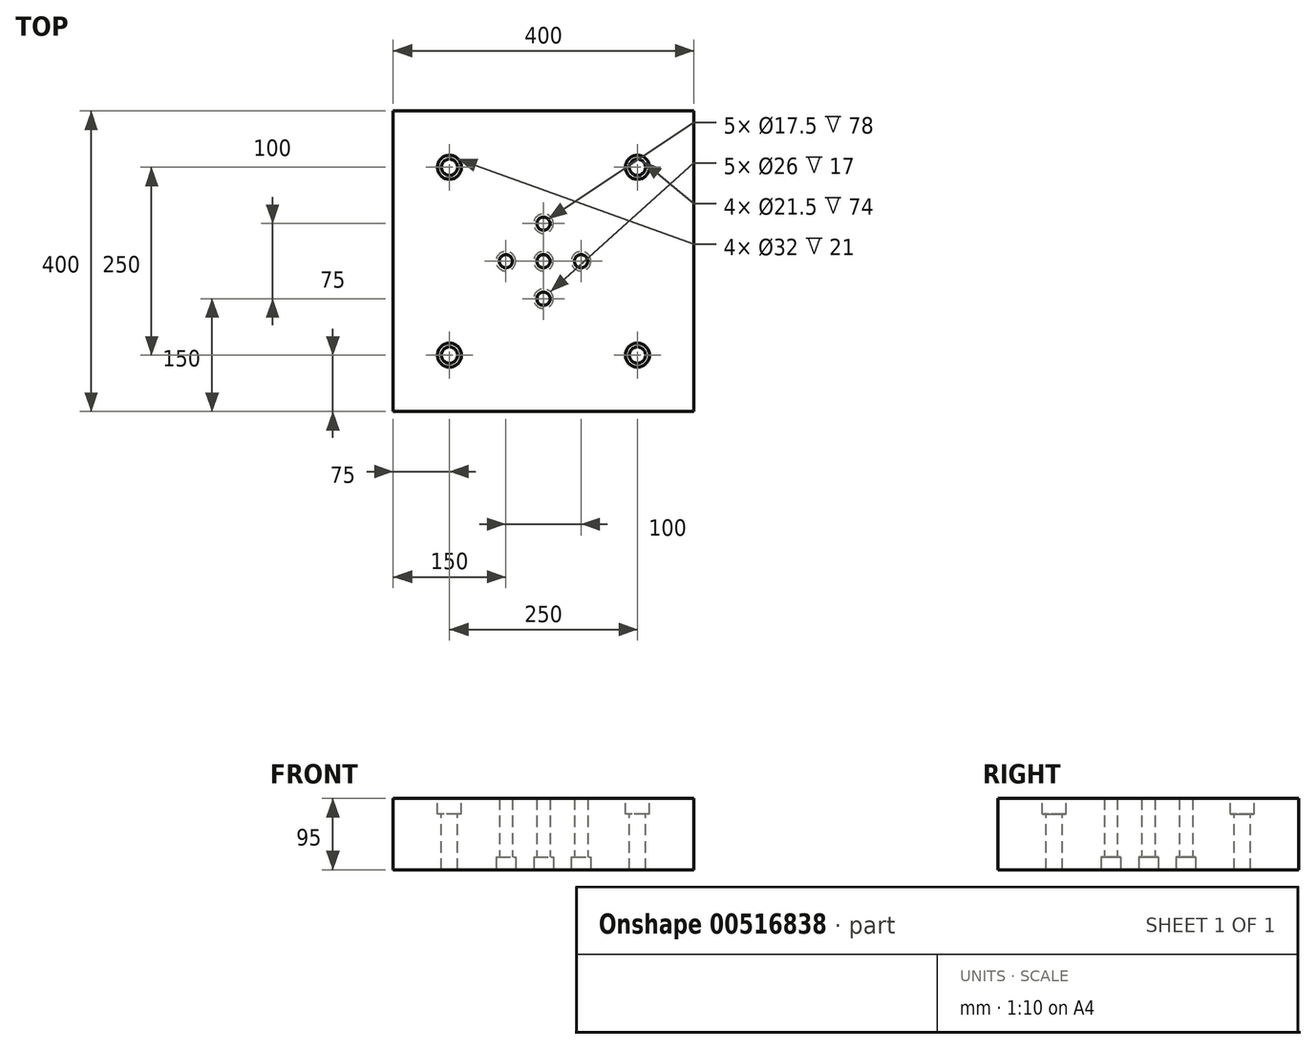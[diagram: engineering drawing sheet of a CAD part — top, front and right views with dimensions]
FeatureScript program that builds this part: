
annotation { "Feature Type Name" : "Feature", "Feature Type Description" : "" }
export const myFeature = defineFeature(function(context is Context, id is Id, definition is map)
    precondition{}
    {
        {
            var Q0;
            Q0=qCreatedBy(makeId("Top.planeOp"),FACE);
            var sketch = newSketch(context, id + "F0", { "sketchPlane" : qUnion([Q0])});
            skLineSegment(sketch, "E0.bottom", {"start": v(-200, 200) * mm, "end": v(200, 200) * mm});
            skLineSegment(sketch, "E0.top", {"start": v(-200, -200) * mm, "end": v(200, -200) * mm});
            skLineSegment(sketch, "E0.left", {"start": v(-200, 200) * mm, "end": v(-200, -200) * mm});
            skLineSegment(sketch, "E0.right", {"start": v(200, 200) * mm, "end": v(200, -200) * mm});
            skSolve(sketch);
        }
        {
            var Q0;
            Q0=makeQuery(id+"F0.imprint","IMPRINT",FACE,{"disambiguationData":[TD([[makeQuery(id+"F0.imprint","IMPRINT",EDGE,{"derivedFrom":sQuery(id+"F0.wireOp",EDGE,"E0.bottom")}),-1.0]])]});
            extrude(context, id + "F1", {"entities" : qUnion([Q0]), "depth" : 95 * mm, "offsetDistance" : 25 * mm});
        }
        {
            var Q0;
            Q0=makeQuery(id+"F1.opExtrude","CAP_FACE",FACE,{"disambiguationData":[OSD([sQuery(id+"F0.wireOp",EDGE,"E0.bottom"),sQuery(id+"F0.wireOp",EDGE,"E0.top"),sQuery(id+"F0.wireOp",EDGE,"E0.left"),sQuery(id+"F0.wireOp",EDGE,"E0.right")])],"isStart":true});
            var sketch = newSketch(context, id + "F2", { "sketchPlane" : qUnion([Q0])});
            skPoint(sketch, "E1", {"position": v(0, 0) * mm});
            skCircle(sketch, "E2", {"center": v(0, 0) * mm, "radius": 50 * mm});
            skPoint(sketch, "E3", {"position": v(0, 50) * mm});
            skPoint(sketch, "E4", {"position": v(-50, 0) * mm});
            skPoint(sketch, "E5", {"position": v(0, -50) * mm});
            skPoint(sketch, "E6", {"position": v(50, 0) * mm});
            skSolve(sketch);
        }
        {
            var Q0;
            Q0=sQuery(id+"F2.wireOp",VERTEX,"E1");
            var Q1;
            Q1=sQuery(id+"F2.wireOp",VERTEX,"E3");
            var Q2;
            Q2=sQuery(id+"F2.wireOp",VERTEX,"E4");
            var Q3;
            Q3=sQuery(id+"F2.wireOp",VERTEX,"E5");
            var Q4;
            Q4=sQuery(id+"F2.wireOp",VERTEX,"E6");
            var Q5;
            Q5=makeQuery(id+"F1.opExtrude","SWEPT_BODY",BODY,{"disambiguationData":[OSD([sQuery(id+"F0.wireOp",EDGE,"E0.bottom"),sQuery(id+"F0.wireOp",EDGE,"E0.top"),sQuery(id+"F0.wireOp",EDGE,"E0.left"),sQuery(id+"F0.wireOp",EDGE,"E0.right")])]});
            hole(context, id + "F3", {"style" : HoleStyle.C_BORE, "endStyle" : HoleEndStyle.THROUGH, "holeDiameter" : 17.5 * mm, "cBoreDiameter" : 26 * mm, "cBoreDepth" : 17 * mm, "isTappedThrough" : true, "tappedDepth" : 12 * mm, "tapClearance" : 3, "startFromSketch" : true, "locations" : qUnion([Q0, Q1, Q2, Q3, Q4]), "scope" : qUnion([Q5])});
        }
        {
            var Q0;
            Q0=makeQuery(id+"F1.opExtrude","CAP_FACE",FACE,{"disambiguationData":[OSD([sQuery(id+"F0.wireOp",EDGE,"E0.bottom"),sQuery(id+"F0.wireOp",EDGE,"E0.top"),sQuery(id+"F0.wireOp",EDGE,"E0.left"),sQuery(id+"F0.wireOp",EDGE,"E0.right")])],"isStart":false});
            var sketch = newSketch(context, id + "F4", { "sketchPlane" : qUnion([Q0])});
            skLineSegment(sketch, "E7.bottom", {"start": v(-125, 125) * mm, "end": v(125, 125) * mm});
            skLineSegment(sketch, "E7.top", {"start": v(-125, -125) * mm, "end": v(125, -125) * mm});
            skLineSegment(sketch, "E7.left", {"start": v(-125, 125) * mm, "end": v(-125, -125) * mm});
            skLineSegment(sketch, "E7.right", {"start": v(125, 125) * mm, "end": v(125, -125) * mm});
            skPoint(sketch, "E8", {"position": v(-125, 125) * mm});
            skPoint(sketch, "E9", {"position": v(125, 125) * mm});
            skPoint(sketch, "E10", {"position": v(125, -125) * mm});
            skPoint(sketch, "E11", {"position": v(-125, -125) * mm});
            skSolve(sketch);
        }
        {
            var Q0;
            Q0=sQuery(id+"F4.wireOp",VERTEX,"E8");
            var Q1;
            Q1=sQuery(id+"F4.wireOp",VERTEX,"E9");
            var Q2;
            Q2=sQuery(id+"F4.wireOp",VERTEX,"E11");
            var Q3;
            Q3=sQuery(id+"F4.wireOp",VERTEX,"E10");
            var Q4;
            Q4=makeQuery(id+"F1.opExtrude","SWEPT_BODY",BODY,{"disambiguationData":[OSD([sQuery(id+"F0.wireOp",EDGE,"E0.bottom"),sQuery(id+"F0.wireOp",EDGE,"E0.top"),sQuery(id+"F0.wireOp",EDGE,"E0.left"),sQuery(id+"F0.wireOp",EDGE,"E0.right")])]});
            hole(context, id + "F5", {"style" : HoleStyle.C_BORE, "endStyle" : HoleEndStyle.THROUGH, "holeDiameter" : 21.5 * mm, "cBoreDiameter" : 32 * mm, "cBoreDepth" : 21 * mm, "isTappedThrough" : true, "tappedDepth" : 12 * mm, "tapClearance" : 3, "startFromSketch" : true, "locations" : qUnion([Q0, Q1, Q2, Q3]), "scope" : qUnion([Q4])});
        }
    });
